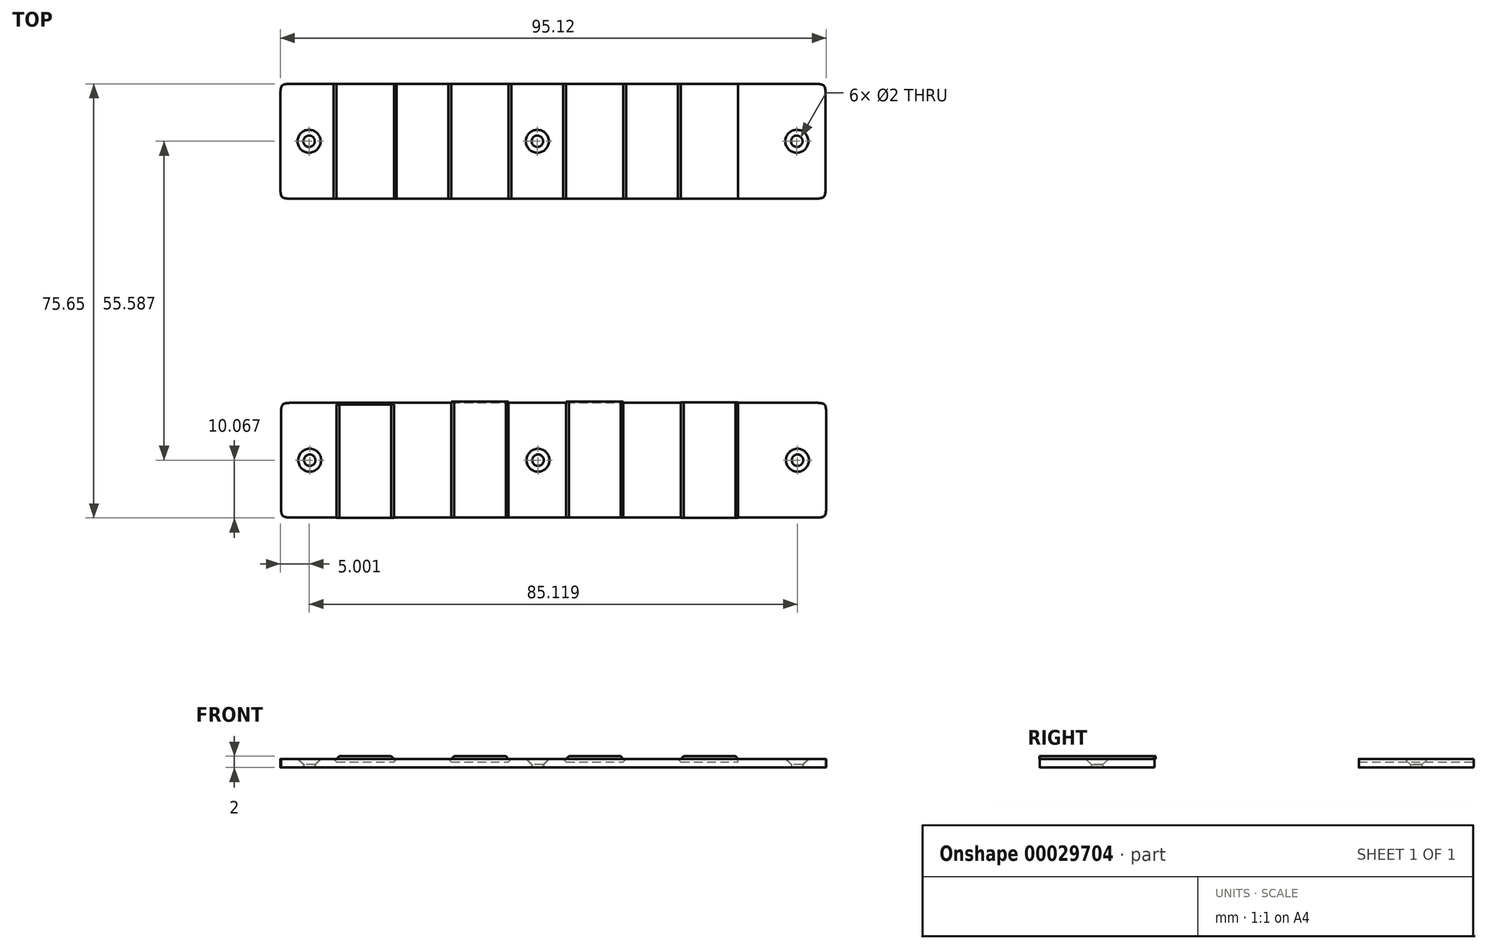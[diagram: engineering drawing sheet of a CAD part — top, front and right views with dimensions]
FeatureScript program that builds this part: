
annotation { "Feature Type Name" : "Feature", "Feature Type Description" : "" }
export const myFeature = defineFeature(function(context is Context, id is Id, definition is map)
    precondition{}
    {
        {
            var Q0;
            Q0=qCreatedBy(makeId("Top.planeOp"),FACE);
            var sketch = newSketch(context, id + "F0", { "sketchPlane" : qUnion([Q0])});
            skCircle(sketch, "E0", {"center": v(0.02, -30.4) * mm, "radius": 1 * mm});
            skCircle(sketch, "E1", {"center": v(45.24, -30.4) * mm, "radius": 1 * mm});
            skPoint(sketch, "E2.centerSnap0", {"position": v(-44.76, -30.4) * mm});
            skCircle(sketch, "E2", {"center": v(-39.76, -30.4) * mm, "radius": 1 * mm});
            skLineSegment(sketch, "E3.right", {"start": v(50.24, -20.4) * mm, "end": v(50.24, -40.4) * mm});
            skLineSegment(sketch, "E3.left", {"start": v(-44.76, -20.4) * mm, "end": v(-44.76, -40.4) * mm});
            skPoint(sketch, "E1.centerSnap0", {"position": v(50.24, -30.4) * mm});
            skLineSegment(sketch, "E3.top", {"start": v(-44.76, -40.4) * mm, "end": v(50.24, -40.4) * mm});
            skLineSegment(sketch, "E3.bottom", {"start": v(-44.76, -20.4) * mm, "end": v(50.24, -20.4) * mm});
            skLineSegment(sketch, "E4.top", {"start": v(-44.88, 15.18) * mm, "end": v(50.12, 15.18) * mm});
            skLineSegment(sketch, "E4.left", {"start": v(-44.88, 35.18) * mm, "end": v(-44.88, 15.18) * mm});
            skPoint(sketch, "E5.centerSnap0", {"position": v(50.12, 25.18) * mm});
            skLineSegment(sketch, "E4.bottom", {"start": v(-44.88, 35.18) * mm, "end": v(50.12, 35.18) * mm});
            skLineSegment(sketch, "E4.right", {"start": v(50.12, 35.18) * mm, "end": v(50.12, 15.18) * mm});
            skPoint(sketch, "E6.centerSnap0", {"position": v(-44.88, 25.18) * mm});
            skCircle(sketch, "E5", {"center": v(45.12, 25.18) * mm, "radius": 1 * mm});
            skCircle(sketch, "E7", {"center": v(-0.1, 25.18) * mm, "radius": 1 * mm});
            skCircle(sketch, "E6", {"center": v(-39.88, 25.18) * mm, "radius": 1 * mm});
            skSolve(sketch);
        }
        {
            var Q0;
            Q0=makeQuery(id+"F0.imprint","IMPRINT",FACE,{"disambiguationData":[TD([[makeQuery(id+"F0.imprint","IMPRINT",EDGE,{"derivedFrom":sQuery(id+"F0.wireOp",EDGE,"E4.top")}),1.0]])]});
            var Q1;
            Q1=makeQuery(id+"F0.imprint","IMPRINT",FACE,{"disambiguationData":[TD([[makeQuery(id+"F0.imprint","IMPRINT",EDGE,{"derivedFrom":sQuery(id+"F0.wireOp",EDGE,"E0")}),-1.0]])]});
            extrude(context, id + "F1", {"entities" : qUnion([Q0, Q1]), "depth" : 1.5 * mm});
        }
        {
            var Q0;
            Q0=makeQuery(id+"F1.opExtrude","SWEPT_EDGE",EDGE,{"disambiguationData":[OSD([sQuery(id+"F0.wireOp",EDGE,"E4.left"),sQuery(id+"F0.wireOp",EDGE,"E4.bottom")])]});
            var Q1;
            Q1=makeQuery(id+"F1.opExtrude","SWEPT_EDGE",EDGE,{"disambiguationData":[OSD([sQuery(id+"F0.wireOp",EDGE,"E4.top"),sQuery(id+"F0.wireOp",EDGE,"E4.left")])]});
            var Q2;
            Q2=makeQuery(id+"F1.opExtrude","SWEPT_EDGE",EDGE,{"disambiguationData":[OSD([sQuery(id+"F0.wireOp",EDGE,"E4.bottom"),sQuery(id+"F0.wireOp",EDGE,"E4.right")])]});
            var Q3;
            Q3=makeQuery(id+"F1.opExtrude","SWEPT_EDGE",EDGE,{"disambiguationData":[OSD([sQuery(id+"F0.wireOp",EDGE,"E4.top"),sQuery(id+"F0.wireOp",EDGE,"E4.right")])]});
            var Q4;
            Q4=makeQuery(id+"F1.opExtrude","SWEPT_EDGE",EDGE,{"disambiguationData":[OSD([sQuery(id+"F0.wireOp",EDGE,"E3.right"),sQuery(id+"F0.wireOp",EDGE,"E3.bottom")])]});
            var Q5;
            Q5=makeQuery(id+"F1.opExtrude","SWEPT_EDGE",EDGE,{"disambiguationData":[OSD([sQuery(id+"F0.wireOp",EDGE,"E3.right"),sQuery(id+"F0.wireOp",EDGE,"E3.top")])]});
            var Q6;
            Q6=makeQuery(id+"F1.opExtrude","SWEPT_EDGE",EDGE,{"disambiguationData":[OSD([sQuery(id+"F0.wireOp",EDGE,"E3.left"),sQuery(id+"F0.wireOp",EDGE,"E3.top")])]});
            var Q7;
            Q7=makeQuery(id+"F1.opExtrude","SWEPT_EDGE",EDGE,{"disambiguationData":[OSD([sQuery(id+"F0.wireOp",EDGE,"E3.left"),sQuery(id+"F0.wireOp",EDGE,"E3.bottom")])]});
            fillet(context, id + "F2", {"entities" : qUnion([Q0, Q1, Q2, Q3, Q4, Q5, Q6, Q7]), "radius" : 2 * mm, "tangentPropagation" : true, "rho" : .7, "crossSection" : FilletCrossSection.CONIC, "allowEdgeOverflow" : false});
        }
        {
            var Q0;
            Q0=makeQuery(id+"F1.opExtrude","CAP_EDGE",EDGE,{"disambiguationData":[OSD([sQuery(id+"F0.wireOp",EDGE,"E6")])],"isStart":false});
            var Q1;
            Q1=makeQuery(id+"F1.opExtrude","CAP_EDGE",EDGE,{"disambiguationData":[OSD([sQuery(id+"F0.wireOp",EDGE,"E7")])],"isStart":false});
            var Q2;
            Q2=makeQuery(id+"F1.opExtrude","CAP_EDGE",EDGE,{"disambiguationData":[OSD([sQuery(id+"F0.wireOp",EDGE,"E5")])],"isStart":false});
            var Q3;
            Q3=makeQuery(id+"F1.opExtrude","CAP_EDGE",EDGE,{"disambiguationData":[OSD([sQuery(id+"F0.wireOp",EDGE,"E2")])],"isStart":false});
            var Q4;
            Q4=makeQuery(id+"F1.opExtrude","CAP_EDGE",EDGE,{"disambiguationData":[OSD([sQuery(id+"F0.wireOp",EDGE,"E1")])],"isStart":false});
            var Q5;
            Q5=makeQuery(id+"F1.opExtrude","CAP_EDGE",EDGE,{"disambiguationData":[OSD([sQuery(id+"F0.wireOp",EDGE,"E0")])],"isStart":false});
            chamfer(context, id + "F3", {"entities" : qUnion([Q0, Q1, Q2, Q3, Q4, Q5]), "width" : 1 * mm, "tangentPropagation" : true});
        }
        {
            var Q0;
            Q0=makeQuery(id+"F1.opExtrude","CAP_FACE",FACE,{"disambiguationData":[OSD([sQuery(id+"F0.wireOp",EDGE,"E4.top"),sQuery(id+"F0.wireOp",EDGE,"E4.left"),sQuery(id+"F0.wireOp",EDGE,"E4.bottom"),sQuery(id+"F0.wireOp",EDGE,"E4.right"),sQuery(id+"F0.wireOp",EDGE,"E5"),sQuery(id+"F0.wireOp",EDGE,"E7"),sQuery(id+"F0.wireOp",EDGE,"E6")])],"isStart":false});
            var sketch = newSketch(context, id + "F4", { "sketchPlane" : qUnion([Q0])});
            skPoint(sketch, "E8.rect.middle", {"position": v(-0.1, 25.18) * mm});
            skLineSegment(sketch, "E9.bottom", {"start": v(-5.1, -20.2) * mm, "end": v(-15.1, -20.2) * mm});
            skLineSegment(sketch, "E9.top", {"start": v(-5.1, -40.42) * mm, "end": v(-15.1, -40.42) * mm});
            skLineSegment(sketch, "E9.left", {"start": v(-5.1, -20.2) * mm, "end": v(-5.1, -40.42) * mm});
            skLineSegment(sketch, "E9.right", {"start": v(-15.1, -20.2) * mm, "end": v(-15.1, -40.42) * mm});
            skLineSegment(sketch, "E10.bottom", {"start": v(24.9, -20.34) * mm, "end": v(34.9, -20.34) * mm});
            skLineSegment(sketch, "E10.top", {"start": v(24.9, -40.47) * mm, "end": v(34.9, -40.47) * mm});
            skLineSegment(sketch, "E10.left", {"start": v(24.9, -20.34) * mm, "end": v(24.9, -40.47) * mm});
            skLineSegment(sketch, "E10.right", {"start": v(34.9, -20.34) * mm, "end": v(34.9, -40.47) * mm});
            skLineSegment(sketch, "E11.bottom", {"start": v(-25.1, -20.68) * mm, "end": v(-35.1, -20.68) * mm});
            skLineSegment(sketch, "E11.top", {"start": v(-25.1, -40.47) * mm, "end": v(-35.1, -40.47) * mm});
            skLineSegment(sketch, "E11.left", {"start": v(-25.1, -20.68) * mm, "end": v(-25.1, -40.47) * mm});
            skLineSegment(sketch, "E11.right", {"start": v(-35.1, -20.68) * mm, "end": v(-35.1, -40.47) * mm});
            skLineSegment(sketch, "E12.bottom", {"start": v(4.9, -20.2) * mm, "end": v(14.9, -20.2) * mm});
            skLineSegment(sketch, "E12.top", {"start": v(4.9, -40.37) * mm, "end": v(14.9, -40.37) * mm});
            skLineSegment(sketch, "E12.left", {"start": v(4.9, -20.2) * mm, "end": v(4.9, -40.37) * mm});
            skLineSegment(sketch, "E12.right", {"start": v(14.9, -20.2) * mm, "end": v(14.9, -40.37) * mm});
            skLineSegment(sketch, "E13.bottom", {"start": v(-35.1, 15.18) * mm, "end": v(-25.1, 15.18) * mm});
            skLineSegment(sketch, "E13.top", {"start": v(-35.1, 35.18) * mm, "end": v(-25.1, 35.18) * mm});
            skLineSegment(sketch, "E13.left", {"start": v(-35.1, 15.18) * mm, "end": v(-35.1, 35.18) * mm});
            skLineSegment(sketch, "E13.right", {"start": v(-25.1, 15.18) * mm, "end": v(-25.1, 35.18) * mm});
            skLineSegment(sketch, "E14.bottom", {"start": v(-15.1, 15.18) * mm, "end": v(-5.1, 15.18) * mm});
            skLineSegment(sketch, "E14.top", {"start": v(-15.1, 35.18) * mm, "end": v(-5.1, 35.18) * mm});
            skLineSegment(sketch, "E14.left", {"start": v(-15.1, 15.18) * mm, "end": v(-15.1, 35.18) * mm});
            skLineSegment(sketch, "E14.right", {"start": v(-5.1, 15.18) * mm, "end": v(-5.1, 35.18) * mm});
            skLineSegment(sketch, "E15.bottom", {"start": v(4.9, 15.18) * mm, "end": v(14.9, 15.18) * mm});
            skLineSegment(sketch, "E15.top", {"start": v(4.9, 35.18) * mm, "end": v(14.9, 35.18) * mm});
            skLineSegment(sketch, "E15.left", {"start": v(4.9, 15.18) * mm, "end": v(4.9, 35.18) * mm});
            skLineSegment(sketch, "E15.right", {"start": v(14.9, 15.18) * mm, "end": v(14.9, 35.18) * mm});
            skLineSegment(sketch, "E16.bottom", {"start": v(24.9, 15.18) * mm, "end": v(34.9, 15.18) * mm});
            skLineSegment(sketch, "E16.top", {"start": v(24.9, 35.18) * mm, "end": v(34.9, 35.18) * mm});
            skLineSegment(sketch, "E16.left", {"start": v(24.9, 15.18) * mm, "end": v(24.9, 35.18) * mm});
            skLineSegment(sketch, "E16.right", {"start": v(34.9, 15.18) * mm, "end": v(34.9, 35.18) * mm});
            skSolve(sketch);
        }
        {
            var Q0;
            Q0=makeQuery(id+"F4.imprint","IMPRINT",FACE,{"disambiguationData":[TD([[makeQuery(id+"F4.imprint","IMPRINT",EDGE,{"derivedFrom":sQuery(id+"F4.wireOp",EDGE,"E11.bottom")}),1.0]])]});
            var Q1;
            Q1=makeQuery(id+"F4.imprint","IMPRINT",FACE,{"disambiguationData":[TD([[makeQuery(id+"F4.imprint","IMPRINT",EDGE,{"derivedFrom":sQuery(id+"F4.wireOp",EDGE,"E9.bottom")}),1.0]])]});
            var Q2;
            Q2=makeQuery(id+"F4.imprint","IMPRINT",FACE,{"disambiguationData":[TD([[makeQuery(id+"F4.imprint","IMPRINT",EDGE,{"derivedFrom":sQuery(id+"F4.wireOp",EDGE,"E12.bottom")}),-1.0]])]});
            var Q3;
            Q3=makeQuery(id+"F4.imprint","IMPRINT",FACE,{"disambiguationData":[TD([[makeQuery(id+"F4.imprint","IMPRINT",EDGE,{"derivedFrom":sQuery(id+"F4.wireOp",EDGE,"E10.bottom")}),-1.0]])]});
            extrude(context, id + "F5", {"entities" : qUnion([Q0, Q1, Q2, Q3]), "depth" : .5 * mm});
        }
        {
            var Q0;
            Q0=makeQuery(id+"F4.imprint","IMPRINT",FACE,{"disambiguationData":[TD([[makeQuery(id+"F4.imprint","IMPRINT",EDGE,{"derivedFrom":sQuery(id+"F4.wireOp",EDGE,"E13.bottom")}),1.0]])]});
            var Q1;
            Q1=makeQuery(id+"F4.imprint","IMPRINT",FACE,{"disambiguationData":[TD([[makeQuery(id+"F4.imprint","IMPRINT",EDGE,{"derivedFrom":sQuery(id+"F4.wireOp",EDGE,"E14.bottom")}),1.0]])]});
            var Q2;
            Q2=makeQuery(id+"F4.imprint","IMPRINT",FACE,{"disambiguationData":[TD([[makeQuery(id+"F4.imprint","IMPRINT",EDGE,{"derivedFrom":sQuery(id+"F4.wireOp",EDGE,"E15.bottom")}),1.0]])]});
            var Q3;
            Q3=makeQuery(id+"F4.imprint","IMPRINT",FACE,{"disambiguationData":[TD([[makeQuery(id+"F4.imprint","IMPRINT",EDGE,{"derivedFrom":sQuery(id+"F4.wireOp",EDGE,"E16.bottom")}),1.0]])]});
            extrude(context, id + "F6", {"entities" : qUnion([Q0, Q1, Q2, Q3]), "operationType" : NewBodyOperationType.REMOVE, "oppositeDirection" : true, "depth" : .5 * mm});
        }
        {
            var Q0;
            Q0=makeQuery(id+"F5.opExtrude","CAP_EDGE",EDGE,{"disambiguationData":[OSD([sQuery(id+"F4.wireOp",EDGE,"E8.rect.right")])],"isStart":false});
            var Q1;
            Q1=makeQuery(id+"F5.opExtrude","CAP_EDGE",EDGE,{"disambiguationData":[OSD([sQuery(id+"F4.wireOp",EDGE,"E8.rect.left")])],"isStart":false});
            var Q2;
            Q2=makeQuery(id+"F5.opExtrude","CAP_EDGE",EDGE,{"disambiguationData":[OSD([sQuery(id+"F4.wireOp",EDGE,"E9.left")])],"isStart":false});
            var Q3;
            Q3=makeQuery(id+"F5.opExtrude","CAP_EDGE",EDGE,{"disambiguationData":[OSD([sQuery(id+"F4.wireOp",EDGE,"E9.right")])],"isStart":false});
            var Q4;
            Q4=makeQuery(id+"F5.opExtrude","CAP_EDGE",EDGE,{"disambiguationData":[OSD([sQuery(id+"F4.wireOp",EDGE,"621597c1-0d24-4cf9-b372-75ebcad5085e.left")])],"isStart":false});
            var Q5;
            Q5=makeQuery(id+"F5.opExtrude","CAP_EDGE",EDGE,{"disambiguationData":[OSD([sQuery(id+"F4.wireOp",EDGE,"621597c1-0d24-4cf9-b372-75ebcad5085e.right")])],"isStart":false});
            var Q6;
            Q6=makeQuery(id+"F5.opExtrude","CAP_EDGE",EDGE,{"disambiguationData":[OSD([sQuery(id+"F4.wireOp",EDGE,"33dbd51d-be97-4ded-bc18-9271b1223188.right")])],"isStart":false});
            var Q7;
            Q7=makeQuery(id+"F5.opExtrude","CAP_EDGE",EDGE,{"disambiguationData":[OSD([sQuery(id+"F4.wireOp",EDGE,"33dbd51d-be97-4ded-bc18-9271b1223188.left")])],"isStart":false});
            var Q8;
            Q8=makeQuery(id+"F5.opExtrude","CAP_EDGE",EDGE,{"disambiguationData":[OSD([sQuery(id+"F4.wireOp",EDGE,"e7b8df1e-ef74-44a0-9be3-0d13bd346d68.left")])],"isStart":false});
            var Q9;
            Q9=makeQuery(id+"F5.opExtrude","CAP_EDGE",EDGE,{"disambiguationData":[OSD([sQuery(id+"F4.wireOp",EDGE,"e7b8df1e-ef74-44a0-9be3-0d13bd346d68.right")])],"isStart":false});
            var Q10;
            Q10=makeQuery(id+"F5.opExtrude","CAP_EDGE",EDGE,{"disambiguationData":[OSD([sQuery(id+"F4.wireOp",EDGE,"E11.left")])],"isStart":false});
            var Q11;
            Q11=makeQuery(id+"F5.opExtrude","CAP_EDGE",EDGE,{"disambiguationData":[OSD([sQuery(id+"F4.wireOp",EDGE,"E11.right")])],"isStart":false});
            var Q12;
            Q12=makeQuery(id+"F5.opExtrude","CAP_EDGE",EDGE,{"disambiguationData":[OSD([sQuery(id+"F4.wireOp",EDGE,"E12.left")])],"isStart":false});
            var Q13;
            Q13=makeQuery(id+"F5.opExtrude","CAP_EDGE",EDGE,{"disambiguationData":[OSD([sQuery(id+"F4.wireOp",EDGE,"E12.right")])],"isStart":false});
            var Q14;
            Q14=makeQuery(id+"F5.opExtrude","CAP_EDGE",EDGE,{"disambiguationData":[OSD([sQuery(id+"F4.wireOp",EDGE,"E10.left")])],"isStart":false});
            var Q15;
            Q15=makeQuery(id+"F5.opExtrude","CAP_EDGE",EDGE,{"disambiguationData":[OSD([sQuery(id+"F4.wireOp",EDGE,"E10.right")])],"isStart":false});
            var Q16;
            Q16=makeQuery(id+"F6.boolean.opBoolean","COPY",EDGE,{"derivedFrom":makeQuery(id+"F6.opExtrude","CAP_EDGE",EDGE,{"disambiguationData":[OSD([sQuery(id+"F4.wireOp",EDGE,"E13.left")])],"isStart":true})});
            var Q17;
            Q17=makeQuery(id+"F6.boolean.opBoolean","COPY",EDGE,{"derivedFrom":makeQuery(id+"F6.opExtrude","CAP_EDGE",EDGE,{"disambiguationData":[OSD([sQuery(id+"F4.wireOp",EDGE,"E13.right")])],"isStart":true})});
            var Q18;
            Q18=makeQuery(id+"F6.boolean.opBoolean","COPY",EDGE,{"derivedFrom":makeQuery(id+"F6.opExtrude","CAP_EDGE",EDGE,{"disambiguationData":[OSD([sQuery(id+"F4.wireOp",EDGE,"E14.left")])],"isStart":true})});
            var Q19;
            Q19=makeQuery(id+"F6.boolean.opBoolean","COPY",EDGE,{"derivedFrom":makeQuery(id+"F6.opExtrude","CAP_EDGE",EDGE,{"disambiguationData":[OSD([sQuery(id+"F4.wireOp",EDGE,"E14.right")])],"isStart":true})});
            var Q20;
            Q20=makeQuery(id+"F6.boolean.opBoolean","COPY",EDGE,{"derivedFrom":makeQuery(id+"F6.opExtrude","CAP_EDGE",EDGE,{"disambiguationData":[OSD([sQuery(id+"F4.wireOp",EDGE,"E15.left")])],"isStart":true})});
            var Q21;
            Q21=makeQuery(id+"F6.boolean.opBoolean","COPY",EDGE,{"derivedFrom":makeQuery(id+"F6.opExtrude","CAP_EDGE",EDGE,{"disambiguationData":[OSD([sQuery(id+"F4.wireOp",EDGE,"E15.right")])],"isStart":true})});
            var Q22;
            Q22=makeQuery(id+"F6.boolean.opBoolean","COPY",EDGE,{"derivedFrom":makeQuery(id+"F6.opExtrude","CAP_EDGE",EDGE,{"disambiguationData":[OSD([sQuery(id+"F4.wireOp",EDGE,"E16.left")])],"isStart":true})});
            var Q23;
            Q23=makeQuery(id+"F6.boolean.opBoolean","COPY",EDGE,{"derivedFrom":makeQuery(id+"F6.opExtrude","CAP_EDGE",EDGE,{"disambiguationData":[OSD([sQuery(id+"F4.wireOp",EDGE,"E16.right")])],"isStart":true})});
            chamfer(context, id + "F7", {"entities" : qUnion([Q0, Q1, Q2, Q3, Q4, Q5, Q6, Q7, Q8, Q9, Q10, Q11, Q12, Q13, Q14, Q15, Q16, Q17, Q18, Q19, Q20, Q21, Q22, Q23]), "width" : .5 * mm, "tangentPropagation" : true});
        }
    });
